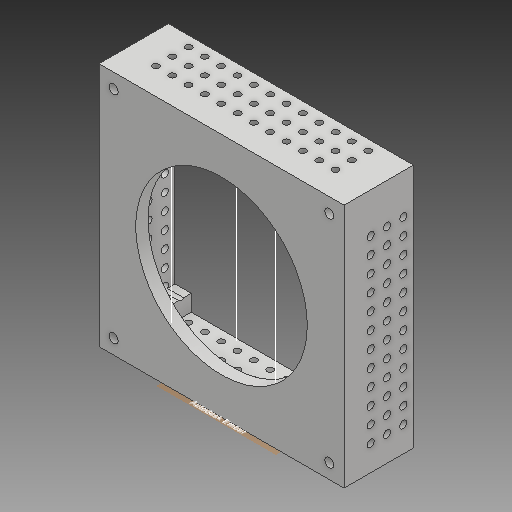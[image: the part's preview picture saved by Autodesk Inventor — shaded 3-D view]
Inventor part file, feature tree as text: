
AUTODESK INVENTOR PART (.ipt)
format: ipt  version: 2018 (Build 220112000, 112)  size: 487,424 bytes
history: native  units: mm
features: sketch x6, extrude x4, pattern_linear x2
ambient origin geometry x8: Origin, YZ Plane, XZ Plane, XY Plane, X Axis, Y Axis, Z Axis, Center Point
bodies: Solid1 (feature_tree)
feature tree (12):
  sketch  "Sketch1"  dims[d0=150.0mm d1=150.0mm]
  extrude  "Extrusion1"  Depth=150.0mm
  extrude  "Extrusion3"  Depth=4.0mm
  extrude  "Extrusion4"  Depth=10.0mm
  pattern_linear  "Rectangular Pattern1"  Count1=2 Spacing1=132.0mm
  extrude  "Extrusion5"  Depth=132.0mm
  pattern_linear  "Rectangular Pattern2"  Count1=8 Spacing1=0.0mm
  sketch  "Sketch9"  dims[d17=20.0mm d19=132.0mm d20=5.5mm d21=80.0mm d22=0.0mm d23=20.0mm d25=132.0mm d26=20.0mm d28=132.0mm]
  sketch  "Sketch2"  dims[d2=7.5mm d3=0.0mm d7=4.0mm]
  sketch  "Sketch4"  dims[d8=35.0mm d9=0.0mm d10=10.0mm]
  sketch  "Sketch5"  dims[d11=10.0mm]
  sketch  "Sketch6"  dims[d12=35.0mm d13=0.0mm d14=20.0mm d16=132.0mm]
